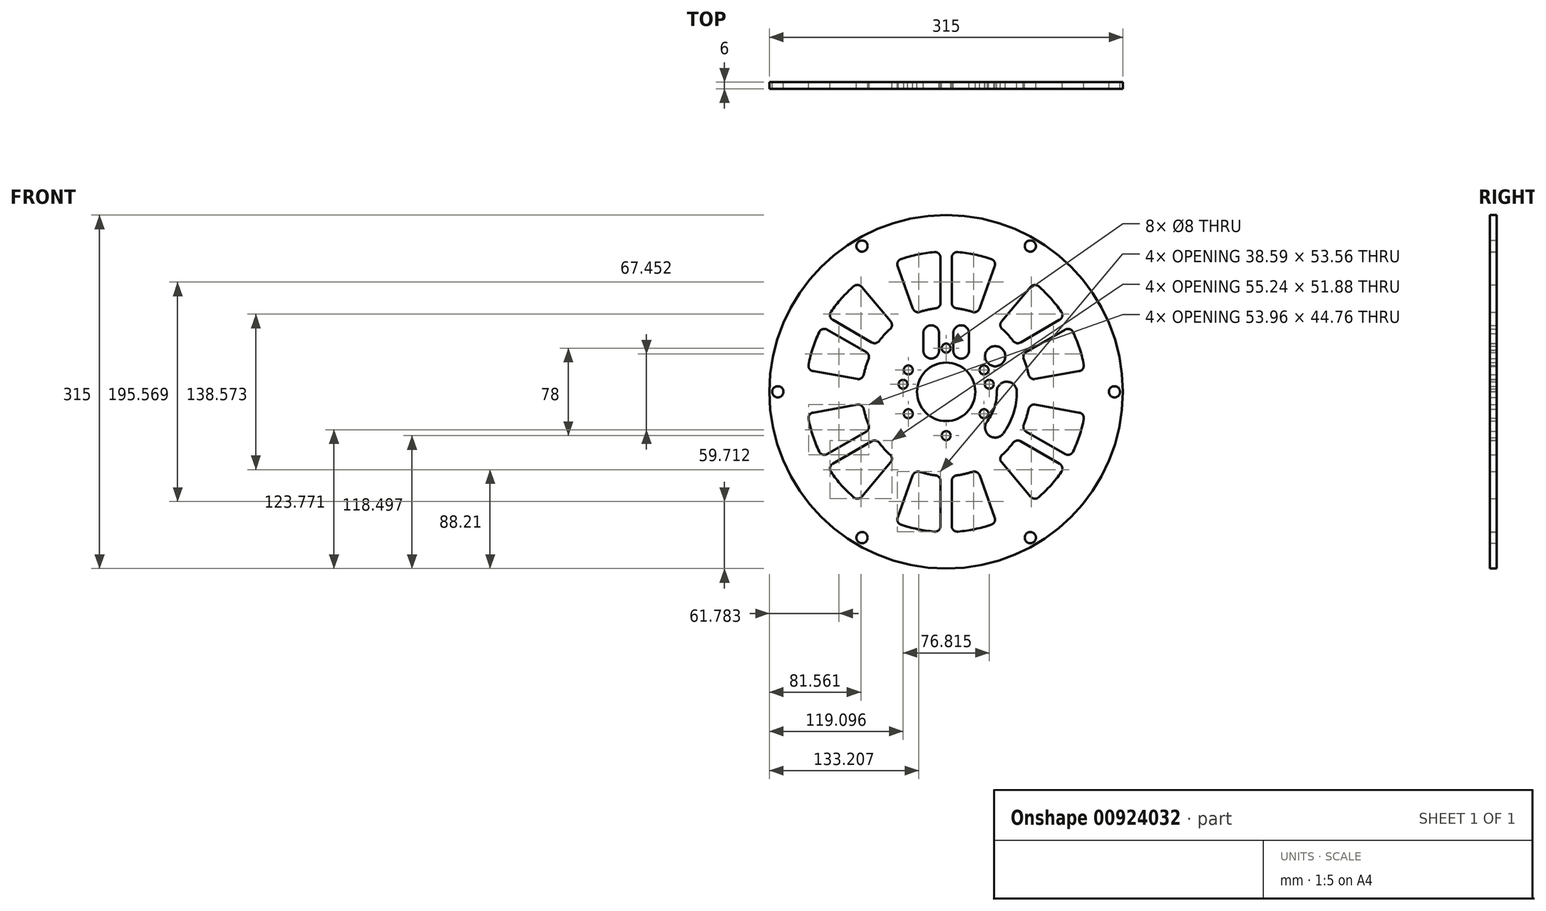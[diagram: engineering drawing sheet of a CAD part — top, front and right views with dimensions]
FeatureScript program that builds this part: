
annotation { "Feature Type Name" : "Feature", "Feature Type Description" : "" }
export const myFeature = defineFeature(function(context is Context, id is Id, definition is map)
    precondition{}
    {
        {
            var Q0;
            Q0=qCreatedBy(makeId("Front.planeOp"),FACE);
            var sketch = newSketch(context, id + "F0", { "sketchPlane" : qUnion([Q0])});
            skCircle(sketch, "E0", {"center": v(55.25, 171.32) * mm, "radius": 26 * mm});
            skCircle(sketch, "E1", {"center": v(55.25, 171.32) * mm, "radius": 39 * mm, "construction": true});
            skCircle(sketch, "E2", {"center": v(55.25, 171.32) * mm, "radius": 62.5 * mm, "construction": true});
            skCircle(sketch, "E3", {"center": v(55.25, 171.32) * mm, "radius": 140 * mm, "construction": true});
            skCircle(sketch, "E4", {"center": v(109.25, 171.32) * mm, "radius": 4.86 * mm, "construction": true});
            skCircle(sketch, "E5", {"center": v(55.25, 171.32) * mm, "radius": 54 * mm, "construction": true});
            skCircle(sketch, "E6.1.0", {"center": v(106.61, 188) * mm, "radius": 4.86 * mm, "construction": true});
            skCircle(sketch, "E6.2.0", {"center": v(98.94, 203.06) * mm, "radius": 4.86 * mm, "construction": true});
            skCircle(sketch, "E6.3.0", {"center": v(87, 215) * mm, "radius": 4.86 * mm, "construction": true});
            skCircle(sketch, "E6.4.0", {"center": v(71.94, 222.67) * mm, "radius": 4.86 * mm, "construction": true});
            skCircle(sketch, "E6.5.0", {"center": v(55.25, 225.32) * mm, "radius": 4.86 * mm, "construction": true});
            skCircle(sketch, "E6.6.0", {"center": v(38.57, 222.67) * mm, "radius": 4.86 * mm, "construction": true});
            skCircle(sketch, "E6.7.0", {"center": v(23.51, 215) * mm, "radius": 4.86 * mm, "construction": true});
            skCircle(sketch, "E6.8.0", {"center": v(11.57, 203.06) * mm, "radius": 4.86 * mm, "construction": true});
            skCircle(sketch, "E6.9.0", {"center": v(3.9, 188) * mm, "radius": 4.86 * mm, "construction": true});
            skCircle(sketch, "E6.10.0", {"center": v(1.25, 171.32) * mm, "radius": 4.86 * mm, "construction": true});
            skCircle(sketch, "E6.11.0", {"center": v(3.9, 154.63) * mm, "radius": 4.86 * mm, "construction": true});
            skCircle(sketch, "E6.12.0", {"center": v(11.57, 139.58) * mm, "radius": 4.86 * mm, "construction": true});
            skCircle(sketch, "E6.13.0", {"center": v(23.51, 127.63) * mm, "radius": 4.86 * mm, "construction": true});
            skCircle(sketch, "E6.14.0", {"center": v(38.57, 119.96) * mm, "radius": 4.86 * mm, "construction": true});
            skCircle(sketch, "E6.15.0", {"center": v(55.25, 117.32) * mm, "radius": 4.86 * mm, "construction": true});
            skCircle(sketch, "E6.16.0", {"center": v(71.94, 119.96) * mm, "radius": 4.86 * mm, "construction": true});
            skCircle(sketch, "E6.17.0", {"center": v(87, 127.63) * mm, "radius": 4.86 * mm, "construction": true});
            skCircle(sketch, "E6.18.0", {"center": v(98.94, 139.58) * mm, "radius": 4.86 * mm, "construction": true});
            skCircle(sketch, "E6.19.0", {"center": v(106.61, 154.63) * mm, "radius": 4.86 * mm, "construction": true});
            skCircle(sketch, "E7", {"center": v(98.94, 203.06) * mm, "radius": 9 * mm});
            skArc(sketch, "E8", {"start": v(118.25, 171.54) * mm, "mid": v(109.35, 180.32) * mm, "end": v(100.26, 171.73) * mm});
            skArc(sketch, "E9", {"start": v(92.07, 145.4) * mm, "mid": v(93.44, 132.45) * mm, "end": v(106.3, 134.4) * mm});
            skCircle(sketch, "E10", {"center": v(55.25, 171.32) * mm, "radius": 157.5 * mm});
            skCircle(sketch, "E11", {"center": v(55.25, 171.32) * mm, "radius": 150 * mm, "construction": true});
            skCircle(sketch, "E12", {"center": v(205.25, 171.32) * mm, "radius": 5 * mm});
            skCircle(sketch, "E13.1.0", {"center": v(130.25, 301.22) * mm, "radius": 5 * mm});
            skCircle(sketch, "E13.2.0", {"center": v(-19.75, 301.22) * mm, "radius": 5 * mm});
            skCircle(sketch, "E13.3.0", {"center": v(-94.75, 171.32) * mm, "radius": 5 * mm});
            skCircle(sketch, "E13.4.0", {"center": v(-19.75, 41.41) * mm, "radius": 5 * mm});
            skCircle(sketch, "E13.5.0", {"center": v(130.25, 41.41) * mm, "radius": 5 * mm});
            skCircle(sketch, "E14", {"center": v(55.25, 210.32) * mm, "radius": 4 * mm});
            skCircle(sketch, "E15.1.0", {"center": v(41.91, 207.97) * mm, "radius": 4 * mm, "construction": true});
            skCircle(sketch, "E15.2.0", {"center": v(30.18, 201.2) * mm, "radius": 4 * mm, "construction": true});
            skCircle(sketch, "E15.3.0", {"center": v(21.48, 190.82) * mm, "radius": 4 * mm});
            skCircle(sketch, "E15.4.0", {"center": v(16.85, 178.09) * mm, "radius": 4 * mm});
            skCircle(sketch, "E15.5.0", {"center": v(16.85, 164.54) * mm, "radius": 4 * mm, "construction": true});
            skCircle(sketch, "E15.6.0", {"center": v(21.48, 151.82) * mm, "radius": 4 * mm});
            skCircle(sketch, "E15.7.0", {"center": v(30.18, 141.44) * mm, "radius": 4 * mm, "construction": true});
            skCircle(sketch, "E15.8.0", {"center": v(41.91, 134.67) * mm, "radius": 4 * mm, "construction": true});
            skCircle(sketch, "E15.9.0", {"center": v(55.25, 132.32) * mm, "radius": 4 * mm});
            skCircle(sketch, "E15.10.0", {"center": v(68.6, 134.67) * mm, "radius": 4 * mm, "construction": true});
            skCircle(sketch, "E15.11.0", {"center": v(80.32, 141.44) * mm, "radius": 4 * mm, "construction": true});
            skCircle(sketch, "E15.12.0", {"center": v(89.03, 151.82) * mm, "radius": 4 * mm});
            skCircle(sketch, "E15.13.0", {"center": v(93.66, 164.54) * mm, "radius": 4 * mm, "construction": true});
            skCircle(sketch, "E15.14.0", {"center": v(93.66, 178.09) * mm, "radius": 4 * mm});
            skCircle(sketch, "E15.15.0", {"center": v(89.03, 190.82) * mm, "radius": 4 * mm});
            skCircle(sketch, "E15.16.0", {"center": v(80.32, 201.2) * mm, "radius": 4 * mm, "construction": true});
            skCircle(sketch, "E15.17.0", {"center": v(68.6, 207.97) * mm, "radius": 4 * mm, "construction": true});
            skArc(sketch, "E16", {"start": v(61.61, 208.67) * mm, "mid": v(68.24, 200.96) * mm, "end": v(75.6, 207.97) * mm});
            skCircle(sketch, "E17", {"center": v(55.25, 171.32) * mm, "radius": 134 * mm, "construction": true});
            skArc(sketch, "E18", {"start": v(95.46, 52.96) * mm, "mid": v(55.25, 296.32) * mm, "end": v(15.04, 52.96) * mm, "construction": true});
            skCircle(sketch, "E19", {"center": v(55.25, 171.32) * mm, "radius": 75 * mm, "construction": true});
            skLineSegment(sketch, "E20", {"start": v(-19.75, 41.41) * mm, "end": v(130.25, 301.22) * mm, "construction": true});
            skLineSegment(sketch, "E21", {"start": v(-19.75, 301.22) * mm, "end": v(130.25, 41.41) * mm, "construction": true});
            skArc(sketch, "E22", {"start": v(31.81, 100.07) * mm, "mid": v(38.77, 98.15) * mm, "end": v(45.88, 96.9) * mm});
            skArc(sketch, "E23", {"start": v(15.04, 52.96) * mm, "mid": v(29.75, 48.95) * mm, "end": v(44.84, 46.75) * mm});
            skLineSegment(sketch, "E24", {"start": v(25.55, 97.02) * mm, "end": v(11.95, 59.4) * mm});
            skLineSegment(sketch, "E25", {"start": v(84.96, 97.02) * mm, "end": v(98.56, 59.4) * mm});
            skLineSegment(sketch, "E26", {"start": v(55.25, 46.32) * mm, "end": v(55.25, 96.32) * mm, "construction": true});
            skLineSegment(sketch, "E27", {"start": v(60.25, 91.94) * mm, "end": v(60.25, 51.73) * mm});
            skLineSegment(sketch, "E28", {"start": v(50.25, 91.94) * mm, "end": v(50.25, 51.73) * mm});
            skArc(sketch, "E29.trimOffspring", {"start": v(64.63, 96.9) * mm, "mid": v(71.74, 98.15) * mm, "end": v(78.7, 100.07) * mm});
            skArc(sketch, "E30.trimOffspring", {"start": v(65.67, 46.75) * mm, "mid": v(80.76, 48.95) * mm, "end": v(95.46, 52.96) * mm});
            skPoint(sketch, "E31.visualSharp", {"position": v(100.25, 54.7) * mm});
            skArc(sketch, "E31.filletArc", {"start": v(95.46, 52.96) * mm, "mid": v(98.36, 55.53) * mm, "end": v(98.56, 59.4) * mm});
            skPoint(sketch, "E32.visualSharp", {"position": v(83.25, 101.74) * mm});
            skArc(sketch, "E32.filletArc", {"start": v(84.96, 97.02) * mm, "mid": v(82.44, 99.82) * mm, "end": v(78.7, 100.07) * mm});
            skPoint(sketch, "E33.visualSharp", {"position": v(27.25, 101.74) * mm});
            skArc(sketch, "E33.filletArc", {"start": v(31.81, 100.07) * mm, "mid": v(28.06, 99.82) * mm, "end": v(25.55, 97.02) * mm});
            skPoint(sketch, "E34.visualSharp", {"position": v(10.25, 54.7) * mm});
            skArc(sketch, "E34.filletArc", {"start": v(11.95, 59.4) * mm, "mid": v(12.15, 55.53) * mm, "end": v(15.04, 52.96) * mm});
            skPoint(sketch, "E35.visualSharp", {"position": v(50.25, 96.48) * mm});
            skArc(sketch, "E35.filletArc", {"start": v(50.25, 91.94) * mm, "mid": v(49, 95.25) * mm, "end": v(45.88, 96.9) * mm});
            skPoint(sketch, "E36.visualSharp", {"position": v(50.25, 46.42) * mm});
            skArc(sketch, "E36.filletArc", {"start": v(44.84, 46.75) * mm, "mid": v(48.64, 48.05) * mm, "end": v(50.25, 51.73) * mm});
            skPoint(sketch, "E37.visualSharp", {"position": v(60.25, 46.42) * mm});
            skArc(sketch, "E37.filletArc", {"start": v(60.25, 51.73) * mm, "mid": v(61.87, 48.05) * mm, "end": v(65.67, 46.75) * mm});
            skPoint(sketch, "E38.visualSharp", {"position": v(60.25, 96.48) * mm});
            skArc(sketch, "E38.filletArc", {"start": v(64.63, 96.9) * mm, "mid": v(61.5, 95.25) * mm, "end": v(60.25, 91.94) * mm});
            skArc(sketch, "E39.trimOffspring", {"start": v(44.84, 46.75) * mm, "mid": v(55.25, 46.32) * mm, "end": v(65.67, 46.75) * mm, "construction": true});
            skArc(sketch, "E40.1.0", {"start": v(105.23, 115.4) * mm, "mid": v(110.38, 120.46) * mm, "end": v(115, 126) * mm});
            skArc(sketch, "E40.1.1", {"start": v(124.38, 142.23) * mm, "mid": v(126.86, 149) * mm, "end": v(128.67, 156) * mm});
            skArc(sketch, "E40.1.2", {"start": v(134.45, 159.9) * mm, "mid": v(130.77, 159.12) * mm, "end": v(128.67, 156) * mm});
            skArc(sketch, "E40.1.3", {"start": v(124.38, 142.23) * mm, "mid": v(124.25, 138.7) * mm, "end": v(126.5, 135.96) * mm});
            skArc(sketch, "E40.1.4", {"start": v(121.5, 127.3) * mm, "mid": v(118, 127.87) * mm, "end": v(115, 126) * mm});
            skLineSegment(sketch, "E40.1.5", {"start": v(121.5, 127.3) * mm, "end": v(156.32, 107.2) * mm});
            skLineSegment(sketch, "E40.1.6", {"start": v(104.74, 108.45) * mm, "end": v(130.53, 77.85) * mm});
            skArc(sketch, "E40.1.7", {"start": v(105.23, 115.4) * mm, "mid": v(103.58, 112.02) * mm, "end": v(104.74, 108.45) * mm});
            skArc(sketch, "E40.1.8", {"start": v(130.53, 77.85) * mm, "mid": v(133.98, 76.1) * mm, "end": v(137.65, 77.32) * mm});
            skArc(sketch, "E40.1.9", {"start": v(137.65, 77.32) * mm, "mid": v(148.48, 88.05) * mm, "end": v(157.92, 100.01) * mm});
            skArc(sketch, "E40.1.10", {"start": v(157.92, 100.01) * mm, "mid": v(158.7, 103.96) * mm, "end": v(156.32, 107.2) * mm});
            skArc(sketch, "E40.1.11", {"start": v(161.32, 115.86) * mm, "mid": v(165.3, 115.41) * mm, "end": v(168.34, 118.06) * mm});
            skLineSegment(sketch, "E40.1.12", {"start": v(126.5, 135.96) * mm, "end": v(161.32, 115.86) * mm});
            skArc(sketch, "E40.1.13", {"start": v(168.34, 118.06) * mm, "mid": v(173.98, 132.22) * mm, "end": v(177.86, 146.96) * mm});
            skLineSegment(sketch, "E40.1.14", {"start": v(134.45, 159.9) * mm, "end": v(173.83, 152.86) * mm});
            skArc(sketch, "E40.1.15", {"start": v(177.86, 146.96) * mm, "mid": v(177.08, 150.75) * mm, "end": v(173.83, 152.86) * mm});
            skArc(sketch, "E40.2.0", {"start": v(128.67, 186.64) * mm, "mid": v(126.86, 193.63) * mm, "end": v(124.38, 200.4) * mm});
            skArc(sketch, "E40.2.1", {"start": v(115, 216.64) * mm, "mid": v(110.38, 222.18) * mm, "end": v(105.23, 227.24) * mm});
            skArc(sketch, "E40.2.2", {"start": v(104.74, 234.19) * mm, "mid": v(103.58, 230.61) * mm, "end": v(105.23, 227.24) * mm});
            skArc(sketch, "E40.2.3", {"start": v(115, 216.64) * mm, "mid": v(118, 214.76) * mm, "end": v(121.5, 215.33) * mm});
            skArc(sketch, "E40.2.4", {"start": v(126.5, 206.67) * mm, "mid": v(124.25, 203.94) * mm, "end": v(124.38, 200.4) * mm});
            skLineSegment(sketch, "E40.2.5", {"start": v(126.5, 206.67) * mm, "end": v(161.32, 226.78) * mm});
            skLineSegment(sketch, "E40.2.6", {"start": v(134.45, 182.74) * mm, "end": v(173.83, 189.78) * mm});
            skArc(sketch, "E40.2.7", {"start": v(128.67, 186.64) * mm, "mid": v(130.77, 183.52) * mm, "end": v(134.45, 182.74) * mm});
            skArc(sketch, "E40.2.8", {"start": v(173.83, 189.78) * mm, "mid": v(177.08, 191.88) * mm, "end": v(177.86, 195.67) * mm});
            skArc(sketch, "E40.2.9", {"start": v(177.86, 195.67) * mm, "mid": v(173.98, 210.42) * mm, "end": v(168.34, 224.58) * mm});
            skArc(sketch, "E40.2.10", {"start": v(168.34, 224.58) * mm, "mid": v(165.3, 227.22) * mm, "end": v(161.32, 226.78) * mm});
            skArc(sketch, "E40.2.11", {"start": v(156.32, 235.44) * mm, "mid": v(158.7, 238.68) * mm, "end": v(157.92, 242.62) * mm});
            skLineSegment(sketch, "E40.2.12", {"start": v(121.5, 215.33) * mm, "end": v(156.32, 235.44) * mm});
            skArc(sketch, "E40.2.13", {"start": v(157.92, 242.62) * mm, "mid": v(148.48, 254.59) * mm, "end": v(137.65, 265.32) * mm});
            skLineSegment(sketch, "E40.2.14", {"start": v(104.74, 234.19) * mm, "end": v(130.53, 264.78) * mm});
            skArc(sketch, "E40.2.15", {"start": v(137.65, 265.32) * mm, "mid": v(133.98, 266.54) * mm, "end": v(130.53, 264.78) * mm});
            skArc(sketch, "E40.3.0", {"start": v(78.7, 242.56) * mm, "mid": v(71.74, 244.48) * mm, "end": v(64.63, 245.73) * mm});
            skArc(sketch, "E40.3.1", {"start": v(45.88, 245.73) * mm, "mid": v(38.77, 244.48) * mm, "end": v(31.81, 242.56) * mm});
            skArc(sketch, "E40.3.2", {"start": v(25.55, 245.61) * mm, "mid": v(28.06, 242.81) * mm, "end": v(31.81, 242.56) * mm});
            skArc(sketch, "E40.3.3", {"start": v(45.88, 245.73) * mm, "mid": v(49, 247.38) * mm, "end": v(50.25, 250.69) * mm});
            skArc(sketch, "E40.3.4", {"start": v(60.25, 250.69) * mm, "mid": v(61.5, 247.38) * mm, "end": v(64.63, 245.73) * mm});
            skLineSegment(sketch, "E40.3.5", {"start": v(60.25, 250.69) * mm, "end": v(60.25, 290.9) * mm});
            skLineSegment(sketch, "E40.3.6", {"start": v(84.96, 245.61) * mm, "end": v(98.56, 283.24) * mm});
            skArc(sketch, "E40.3.7", {"start": v(78.7, 242.56) * mm, "mid": v(82.44, 242.81) * mm, "end": v(84.96, 245.61) * mm});
            skArc(sketch, "E40.3.8", {"start": v(98.56, 283.24) * mm, "mid": v(98.36, 287.1) * mm, "end": v(95.46, 289.67) * mm});
            skArc(sketch, "E40.3.9", {"start": v(95.46, 289.67) * mm, "mid": v(80.76, 293.69) * mm, "end": v(65.67, 295.88) * mm});
            skArc(sketch, "E40.3.10", {"start": v(65.67, 295.88) * mm, "mid": v(61.87, 294.58) * mm, "end": v(60.25, 290.9) * mm});
            skArc(sketch, "E40.3.11", {"start": v(50.25, 290.9) * mm, "mid": v(48.64, 294.58) * mm, "end": v(44.84, 295.88) * mm});
            skLineSegment(sketch, "E40.3.12", {"start": v(50.25, 250.69) * mm, "end": v(50.25, 290.9) * mm});
            skArc(sketch, "E40.3.13", {"start": v(44.84, 295.88) * mm, "mid": v(29.75, 293.69) * mm, "end": v(15.04, 289.67) * mm});
            skLineSegment(sketch, "E40.3.14", {"start": v(25.55, 245.61) * mm, "end": v(11.95, 283.24) * mm});
            skArc(sketch, "E40.3.15", {"start": v(15.04, 289.67) * mm, "mid": v(12.15, 287.1) * mm, "end": v(11.95, 283.24) * mm});
            skArc(sketch, "E40.4.0", {"start": v(5.27, 227.24) * mm, "mid": v(0.13, 222.18) * mm, "end": v(-4.5, 216.64) * mm});
            skArc(sketch, "E40.4.1", {"start": v(-13.88, 200.4) * mm, "mid": v(-16.35, 193.63) * mm, "end": v(-18.16, 186.64) * mm});
            skArc(sketch, "E40.4.2", {"start": v(-23.94, 182.74) * mm, "mid": v(-20.26, 183.52) * mm, "end": v(-18.16, 186.64) * mm});
            skArc(sketch, "E40.4.3", {"start": v(-13.88, 200.4) * mm, "mid": v(-13.75, 203.94) * mm, "end": v(-15.99, 206.67) * mm});
            skArc(sketch, "E40.4.4", {"start": v(-10.99, 215.33) * mm, "mid": v(-7.5, 214.76) * mm, "end": v(-4.5, 216.64) * mm});
            skLineSegment(sketch, "E40.4.5", {"start": v(-10.99, 215.33) * mm, "end": v(-45.8, 235.44) * mm});
            skLineSegment(sketch, "E40.4.6", {"start": v(5.77, 234.19) * mm, "end": v(-20.02, 264.78) * mm});
            skArc(sketch, "E40.4.7", {"start": v(5.27, 227.24) * mm, "mid": v(6.93, 230.61) * mm, "end": v(5.77, 234.19) * mm});
            skArc(sketch, "E40.4.8", {"start": v(-20.02, 264.78) * mm, "mid": v(-23.47, 266.54) * mm, "end": v(-27.14, 265.32) * mm});
            skArc(sketch, "E40.4.9", {"start": v(-27.14, 265.32) * mm, "mid": v(-37.97, 254.59) * mm, "end": v(-47.41, 242.62) * mm});
            skArc(sketch, "E40.4.10", {"start": v(-47.41, 242.62) * mm, "mid": v(-48.19, 238.68) * mm, "end": v(-45.8, 235.44) * mm});
            skArc(sketch, "E40.4.11", {"start": v(-50.8, 226.78) * mm, "mid": v(-54.8, 227.22) * mm, "end": v(-57.83, 224.58) * mm});
            skLineSegment(sketch, "E40.4.12", {"start": v(-15.99, 206.67) * mm, "end": v(-50.8, 226.78) * mm});
            skArc(sketch, "E40.4.13", {"start": v(-57.83, 224.58) * mm, "mid": v(-63.47, 210.42) * mm, "end": v(-67.35, 195.67) * mm});
            skLineSegment(sketch, "E40.4.14", {"start": v(-23.94, 182.74) * mm, "end": v(-63.33, 189.78) * mm});
            skArc(sketch, "E40.4.15", {"start": v(-67.35, 195.67) * mm, "mid": v(-66.58, 191.88) * mm, "end": v(-63.33, 189.78) * mm});
            skArc(sketch, "E40.5.0", {"start": v(-18.16, 156) * mm, "mid": v(-16.35, 149) * mm, "end": v(-13.88, 142.23) * mm});
            skArc(sketch, "E40.5.1", {"start": v(-4.5, 126) * mm, "mid": v(0.13, 120.46) * mm, "end": v(5.27, 115.4) * mm});
            skArc(sketch, "E40.5.2", {"start": v(5.77, 108.45) * mm, "mid": v(6.93, 112.02) * mm, "end": v(5.27, 115.4) * mm});
            skArc(sketch, "E40.5.3", {"start": v(-4.5, 126) * mm, "mid": v(-7.5, 127.87) * mm, "end": v(-10.99, 127.3) * mm});
            skArc(sketch, "E40.5.4", {"start": v(-15.99, 135.96) * mm, "mid": v(-13.75, 138.7) * mm, "end": v(-13.88, 142.23) * mm});
            skLineSegment(sketch, "E40.5.5", {"start": v(-15.99, 135.96) * mm, "end": v(-50.8, 115.86) * mm});
            skLineSegment(sketch, "E40.5.6", {"start": v(-23.94, 159.9) * mm, "end": v(-63.33, 152.86) * mm});
            skArc(sketch, "E40.5.7", {"start": v(-18.16, 156) * mm, "mid": v(-20.26, 159.12) * mm, "end": v(-23.94, 159.9) * mm});
            skArc(sketch, "E40.5.8", {"start": v(-63.33, 152.86) * mm, "mid": v(-66.58, 150.75) * mm, "end": v(-67.35, 146.96) * mm});
            skArc(sketch, "E40.5.9", {"start": v(-67.35, 146.96) * mm, "mid": v(-63.47, 132.22) * mm, "end": v(-57.83, 118.06) * mm});
            skArc(sketch, "E40.5.10", {"start": v(-57.83, 118.06) * mm, "mid": v(-54.8, 115.41) * mm, "end": v(-50.8, 115.86) * mm});
            skArc(sketch, "E40.5.11", {"start": v(-45.8, 107.2) * mm, "mid": v(-48.19, 103.96) * mm, "end": v(-47.41, 100.01) * mm});
            skLineSegment(sketch, "E40.5.12", {"start": v(-10.99, 127.3) * mm, "end": v(-45.8, 107.2) * mm});
            skArc(sketch, "E40.5.13", {"start": v(-47.41, 100.01) * mm, "mid": v(-37.97, 88.05) * mm, "end": v(-27.14, 77.32) * mm});
            skLineSegment(sketch, "E40.5.14", {"start": v(5.77, 108.45) * mm, "end": v(-20.02, 77.85) * mm});
            skArc(sketch, "E40.5.15", {"start": v(-27.14, 77.32) * mm, "mid": v(-23.47, 76.1) * mm, "end": v(-20.02, 77.85) * mm});
            skArc(sketch, "E41", {"start": v(37.12, 213.05) * mm, "mid": v(67.61, 127.53) * mm, "end": v(48.9, 216.37) * mm, "construction": true});
            skArc(sketch, "E42", {"start": v(106.26, 134.34) * mm, "mid": v(115.17, 152) * mm, "end": v(118.25, 171.54) * mm});
            skArc(sketch, "E43", {"start": v(92.07, 145.4) * mm, "mid": v(98.35, 157.88) * mm, "end": v(100.26, 171.73) * mm});
            skArc(sketch, "E44", {"start": v(48.9, 223.17) * mm, "mid": v(41.88, 230.64) * mm, "end": v(34.94, 223.1) * mm});
            skArc(sketch, "E45", {"start": v(75.6, 223.23) * mm, "mid": v(68.82, 230.64) * mm, "end": v(61.6, 223.64) * mm});
            skLineSegment(sketch, "E46", {"start": v(61.61, 207.26) * mm, "end": v(61.6, 224.94) * mm});
            skLineSegment(sketch, "E47", {"start": v(75.6, 224.07) * mm, "end": v(75.6, 207.97) * mm});
            skLineSegment(sketch, "E48", {"start": v(48.9, 224.11) * mm, "end": v(48.9, 208.63) * mm});
            skLineSegment(sketch, "E49", {"start": v(34.94, 224.18) * mm, "end": v(34.94, 207.7) * mm});
            skArc(sketch, "E50.trimOffspring", {"start": v(34.94, 208.23) * mm, "mid": v(42.13, 200.97) * mm, "end": v(48.9, 208.63) * mm});
            skSolve(sketch);
        }
        {
            var Q0;
            Q0=makeQuery(id+"F0.imprint","IMPRINT",FACE,{"disambiguationData":[TD([[makeQuery(id+"F0.imprint","IMPRINT",EDGE,{"derivedFrom":sQuery(id+"F0.wireOp",EDGE,"E0")}),-1.0]])]});
            extrude(context, id + "F1", {"entities" : qUnion([Q0]), "depth" : 6 * mm, "offsetDistance" : 25 * mm});
        }
    });
